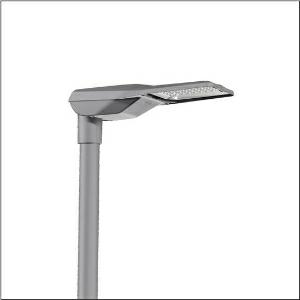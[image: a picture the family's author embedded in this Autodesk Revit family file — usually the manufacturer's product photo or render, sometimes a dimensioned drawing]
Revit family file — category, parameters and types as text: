
# Revit family: streetlight_sl_21_iq_mini___st0_8a_5xe2c31g08jb_bdc9
name_source: partatom
category: Lighting Fixtures
units: mm (PartAtom-declared; Revit-internal decimal feet)

## family parameters
Cut with Voids When Loaded = No
Host = Face
Light Source = No
Part Type = Normal
Room Calculation Point = No
Round Connector Dimension = Use Diameter
Shared = No

## types (1)
- --- (1 x LED, 10820 lm, 71.6 W, 3000K)
    Apparent Load = 72 VA
    CIE Flux Codes = 41 75 97 100 100
    Color Rendering = 70
    Color Temperature = 3000K
    Default Elevation = 1800 mm
    Description = Streetlight SL 21 iQ mini, mast luminaire, primary light control with lens, of PMMA, primary optical cover: cover, of toughened safety glass, transparent, light distribution: ST0.8a, light emission: direct distribution, primary light characteristic: asymmetric, installation type: post-top, side-entry, LED, High Power LED, rated luminous flux: 10.820lm, luminous efficacy: 151lm/W, light colour: 730, colour temperature: 3000K, control gear: iQ Street-Remote, control: Street-Remote, Auto-Match, Temp-Guard, Lumen-Switch, Night-Set, Smart-Wire, Light-Fading, Desk-Remote (wireless, voltage-free reading and setting of iQ features in the workshop via application-optimized NFC function/RFID function), optimised constant luminous flux control (CLO 2.0), pre-setting: linear dimming characteristic, mains connection: 220..240V, AC, 50/60Hz, start of lifetime: 72W, end of service life: 75W, reduction: 33W, luminaire housing, of diecast aluminium, powder-coated, Siteco® metallic grey (DB 702S), corrosivity category C5 mid according to DIN EN ISO 12944, please order mast flange separately, inclination adjustable: 0°, 5°, 10°, 15°, sealing non-destructively replaceable, multi-level sealing system, length: 628mm, width: 235mm, height: 110mm, mast flange for spigot size: 42mm (side-entry): 5XC10008XM4, 60/48mm (side-entry/post-top): 5XC10108XM2, 76/60mm (side-entry/post-top): 5XC10108XM1, mounting height: 4..8m, protection rating (complete): IP66, insulation class (complete): insulation class II (safety insulation), certification: CE, ENEC, ENEC+, VDE, impact resistance: IK10, permissible operating ambient temperature for outdoor applications: -40..+50°C, standard-compliant lighting for roads and squares, packaging unit: 1 piece

Light Distribution: ST0.8a
    Height = 110 mm
    Lamp = 1 x LED
    Lamp Light Flux = 10820 lm
    Lamp Power = 71.6 W
    Lamp count = 1
    Length = 625 mm
    Luminous efficacy = 151 lm/W
    Manufacturer = Siteco
    ModVariant = No
    Model = 5XE2C31G08JB
    Number of Poles = 1
    OnlyDefault = Yes
    Power Factor = 1
    Product Name = Streetlight SL 21 iQ mini | ST0.8a
    Product group = mast luminaire | pylon top
    ProductGroupID = 6100
    Protection Class = Protection class II
    Protection Degree = IP 66
    RLX_Detail_Level = 1
    RLX_Emergency_Light_Flux = 0 lm
    RLX_Emergency_Type = 0
    RLX_Emergency_Type_DB = No
    RlxData = <blob elided: 26345 chars, md5=7ee4cf86>
    Socket = socket
    Standby Power = 0 W
    System Light Flux = 10820 lm
    System Power = 72 W
    Type Comments = factory setting: luminous flux: 100 % | dim-lin: 254 | 746 mA
    Type Image = l_1003519.jpg
    URL = http://relux.com
    VarID = @adj_190733
    Voltage = 0 V
    Weight = 0.00 kg
    Width = 234 mm

## geometry (parser evidence)
native form markers: Blend x4, Sweep x13
no freeform markers — native parametric forms only
